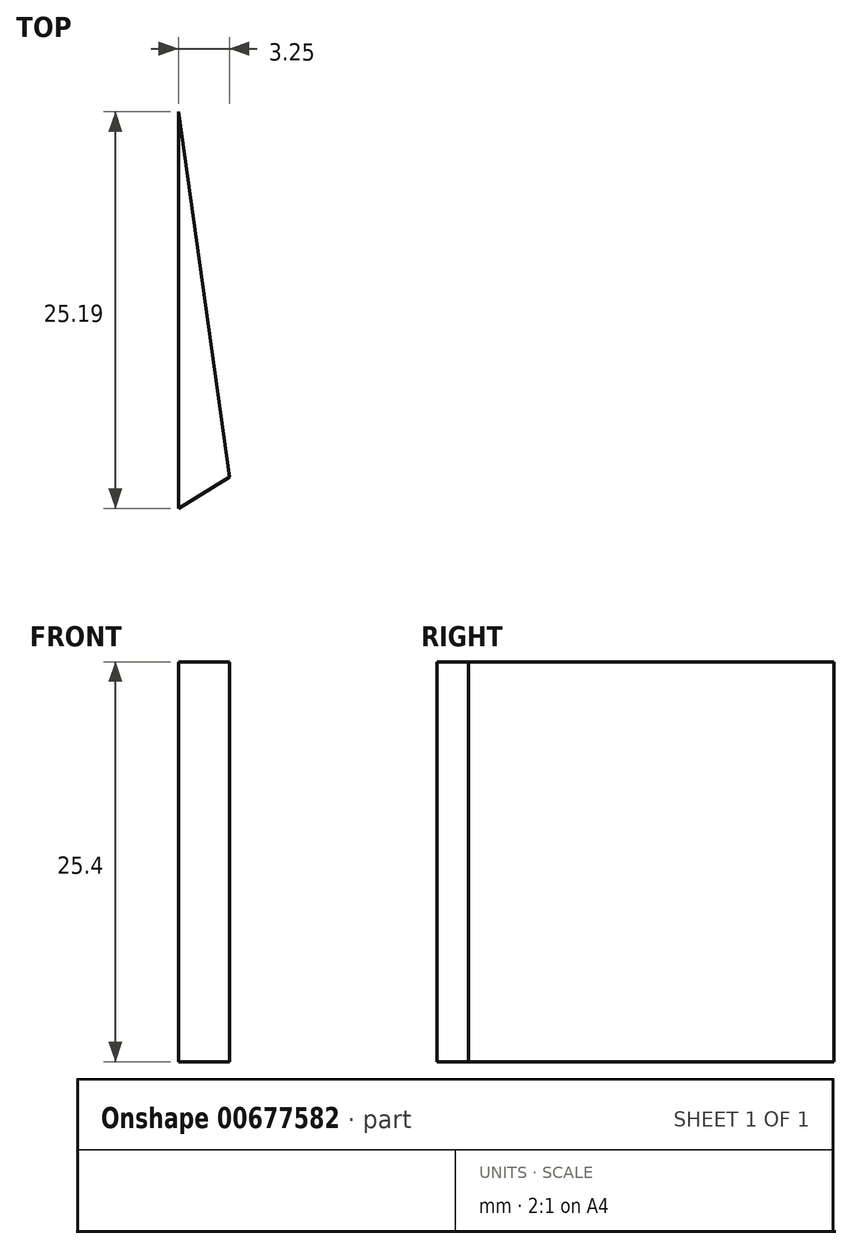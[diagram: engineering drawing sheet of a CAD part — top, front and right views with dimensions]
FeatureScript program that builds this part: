
annotation { "Feature Type Name" : "Feature", "Feature Type Description" : "" }
export const myFeature = defineFeature(function(context is Context, id is Id, definition is map)
    precondition{}
    {
        {
            var Q0;
            Q0=qCreatedBy(makeId("Top.planeOp"),FACE);
            var sketch = newSketch(context, id + "F0", { "sketchPlane" : qUnion([Q0])});
            skLineSegment(sketch, "E0", {"start": v(29.38, -36.56) * mm, "end": v(26.99, -28.5) * mm});
            skLineSegment(sketch, "E1", {"start": v(26.99, -28.5) * mm, "end": v(25.05, -24.93) * mm});
            skLineSegment(sketch, "E2", {"start": v(25.05, -24.93) * mm, "end": v(22, -22.18) * mm});
            skLineSegment(sketch, "E3", {"start": v(22, -22.18) * mm, "end": v(18.05, -19.72) * mm});
            skLineSegment(sketch, "E4", {"start": v(18.05, -19.72) * mm, "end": v(11.1, -16.7) * mm});
            skLineSegment(sketch, "E5", {"start": v(11.1, -16.7) * mm, "end": v(11.1, -15.91) * mm});
            skLineSegment(sketch, "E6", {"start": v(11.1, -15.54) * mm, "end": v(12.97, -14.83) * mm});
            skLineSegment(sketch, "E7", {"start": v(12.97, -14.83) * mm, "end": v(14.38, -12.83) * mm});
            skLineSegment(sketch, "E8", {"start": v(14.38, -12.83) * mm, "end": v(15.1, -11.8) * mm});
            skLineSegment(sketch, "E9", {"start": v(15.1, -11.8) * mm, "end": v(16.37, -10.53) * mm});
            skLineSegment(sketch, "E10", {"start": v(16.37, -10.53) * mm, "end": v(18.26, -6.19) * mm});
            skLineSegment(sketch, "E11", {"start": v(18.26, -6.19) * mm, "end": v(19.81, -1.07) * mm});
            skLineSegment(sketch, "E12", {"start": v(19.81, -1.07) * mm, "end": v(20.7, 3.06) * mm});
            skLineSegment(sketch, "E13", {"start": v(20.7, 3.06) * mm, "end": v(21.81, 5.63) * mm});
            skLineSegment(sketch, "E14", {"start": v(21.81, 5.63) * mm, "end": v(23.06, 8.49) * mm});
            skLineSegment(sketch, "E15", {"start": v(23.06, 8.49) * mm, "end": v(-10.13, -11.8) * mm});
            skLineSegment(sketch, "E16", {"start": v(-10.13, -11.8) * mm, "end": v(-10.13, 13.4) * mm});
            skLineSegment(sketch, "E17", {"start": v(-10.13, 13.4) * mm, "end": v(-4.03, -30.19) * mm});
            skLineSegment(sketch, "E18", {"start": v(-4.03, -30.19) * mm, "end": v(11.1, -17.45) * mm});
            skSolve(sketch);
        }
        {
            var Q0;
            Q0 = qSketchRegion(id + "F0", true);
            extrude(context, id + "F1", {"entities" : qUnion([Q0]), "depth" : 25.4 * mm, "offsetDistance" : 25.4 * mm});
        }
    });
